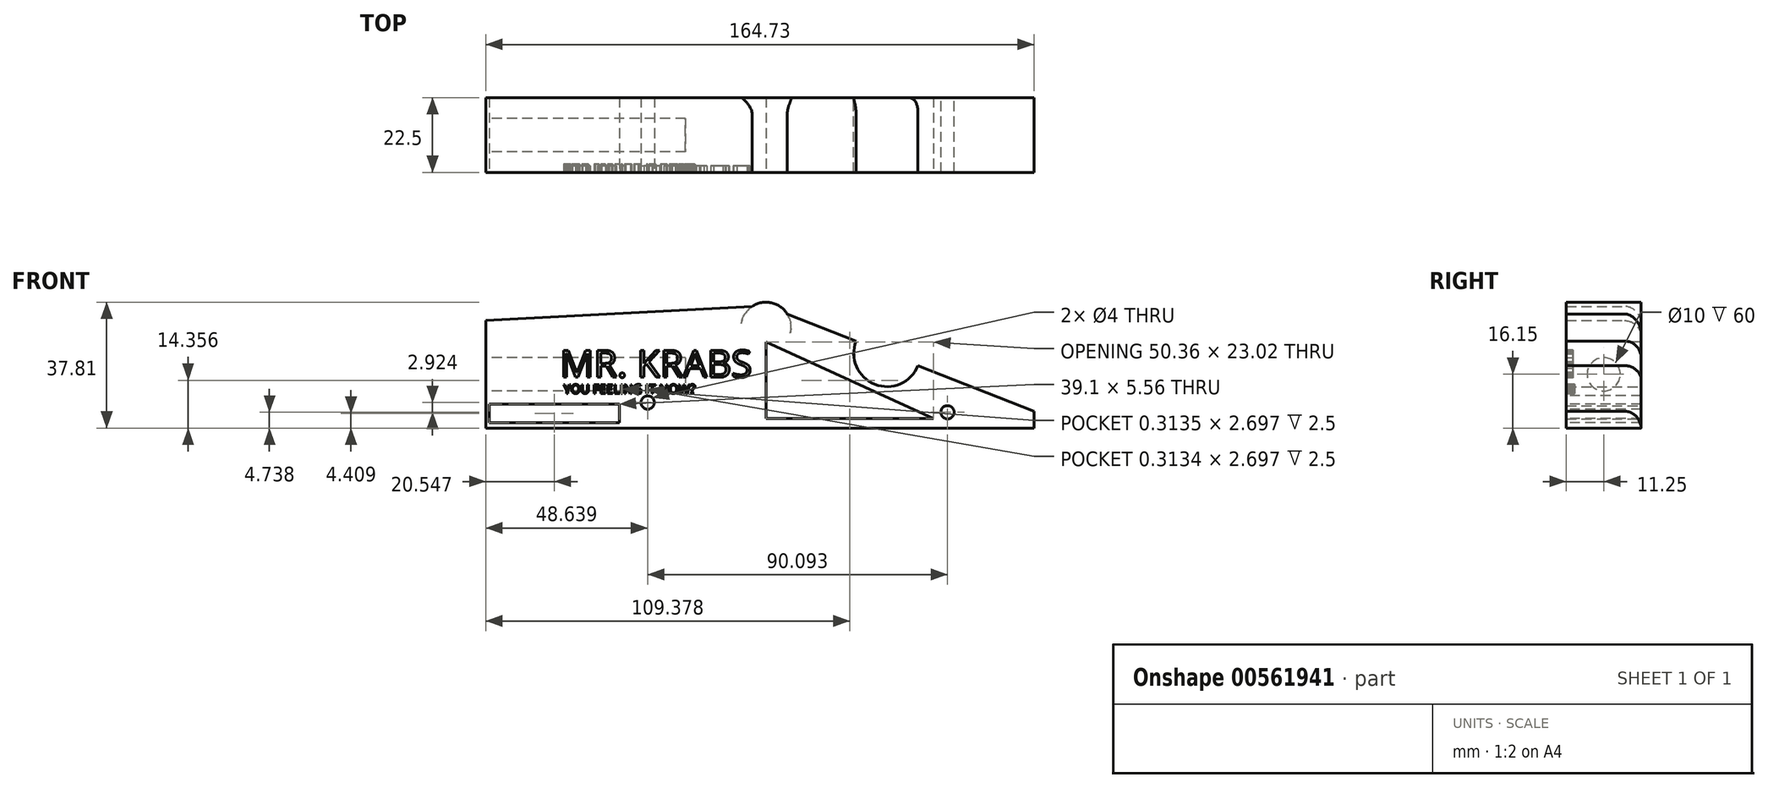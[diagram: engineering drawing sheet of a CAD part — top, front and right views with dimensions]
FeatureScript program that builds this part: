
annotation { "Feature Type Name" : "Feature", "Feature Type Description" : "" }
export const myFeature = defineFeature(function(context is Context, id is Id, definition is map)
    precondition{}
    {
        {
            var Q0;
            Q0=qCreatedBy(makeId("Front.planeOp"),FACE);
            var sketch = newSketch(context, id + "F0", { "sketchPlane" : qUnion([Q0])});
            skLineSegment(sketch, "E0.bottom", {"start": v(-84.2, -32.3) * mm, "end": v(215.8, -32.3) * mm});
            skLineSegment(sketch, "E0.top", {"start": v(-84.2, 37.7) * mm, "end": v(215.8, 37.7) * mm});
            skLineSegment(sketch, "E0.left", {"start": v(-84.2, -32.3) * mm, "end": v(-84.2, 37.7) * mm});
            skLineSegment(sketch, "E0.right", {"start": v(215.8, -32.3) * mm, "end": v(215.8, 37.7) * mm});
            skLineSegment(sketch, "E1", {"start": v(0, 4.48) * mm, "end": v(80.53, -27.27) * mm});
            skLineSegment(sketch, "E2", {"start": v(80.53, -27.27) * mm, "end": v(80.53, -32.3) * mm});
            skLineSegment(sketch, "E3", {"start": v(0, 4.48) * mm, "end": v(-84.2, 0) * mm});
            skPoint(sketch, "E3.endSnap0", {"position": v(-84.2, 2.7) * mm});
            skSolve(sketch);
        }
        {
            var Q0;
            Q0=makeQuery(id+"F0.imprint","IMPRINT",FACE,{"disambiguationData":[TD([[makeQuery(id+"F0.imprint","IMPRINT",EDGE,{"derivedFrom":sQuery(id+"F0.wireOp",EDGE,"E0.bottom")}),1.0]])]});
            extrude(context, id + "F1", {"entities" : qUnion([Q0]), "depth" : 40 * mm});
        }
        {
            var Q0;
            Q0=makeQuery(id+"F1.opExtrude","CAP_FACE",FACE,{"disambiguationData":[OSD([sQuery(id+"F0.wireOp",EDGE,"E0.bottom"),sQuery(id+"F0.wireOp",EDGE,"E0.top"),sQuery(id+"F0.wireOp",EDGE,"E0.left"),sQuery(id+"F0.wireOp",EDGE,"E0.right")])],"isStart":false});
            var sketch = newSketch(context, id + "F2", { "sketchPlane" : qUnion([Q0])});
            skCircle(sketch, "E4", {"center": v(-35.56, -24.64) * mm, "radius": 2 * mm});
            skCircle(sketch, "E5", {"center": v(174.33, -24.64) * mm, "radius": 2 * mm});
            skSolve(sketch);
        }
        {
            var Q0;
            Q0=makeQuery(id+"F2.imprint","IMPRINT",FACE,{"disambiguationData":[TD([[makeQuery(id+"F2.imprint","IMPRINT",EDGE,{"derivedFrom":sQuery(id+"F2.wireOp",EDGE,"E4")}),1.0]])]});
            var Q1;
            Q1=makeQuery(id+"F2.imprint","IMPRINT",FACE,{"disambiguationData":[TD([[makeQuery(id+"F2.imprint","IMPRINT",EDGE,{"derivedFrom":sQuery(id+"F2.wireOp",EDGE,"E5")}),1.0]])]});
            extrude(context, id + "F3", {"entities" : qUnion([Q0, Q1]), "operationType" : NewBodyOperationType.REMOVE, "endBound" : BoundingType.THROUGH_ALL, "oppositeDirection" : true, "depth" : 25 * mm});
        }
        {
            var Q0;
            Q0=makeQuery(id+"F2.imprint","IMPRINT",FACE,{"disambiguationData":[TD([[makeQuery(id+"F2.imprint","IMPRINT",EDGE,{"derivedFrom":sQuery(id+"F2.wireOp",EDGE,"E4")}),-1.0]])]});
            extrude(context, id + "F4", {"entities" : qUnion([Q0]), "operationType" : NewBodyOperationType.REMOVE, "oppositeDirection" : true, "depth" : 17.5 * mm, "offsetDistance" : 25 * mm});
        }
        {
            var Q0;
            Q0=makeQuery(id+"F1.opExtrude","SWEPT_FACE",FACE,{"disambiguationData":[OSD([sQuery(id+"F0.wireOp",EDGE,"E0.left")])]});
            var sketch = newSketch(context, id + "F5", { "sketchPlane" : qUnion([Q0])});
            skCircle(sketch, "E6", {"center": v(11.25, -16.15) * mm, "radius": 5 * mm});
            skPoint(sketch, "E6.centerSnap0", {"position": v(0, -16.15) * mm});
            skPoint(sketch, "E6.centerSnap1", {"position": v(11.25, -32.3) * mm});
            skSolve(sketch);
        }
        {
            var Q0;
            Q0=makeQuery(id+"F5.imprint","IMPRINT",FACE,{"disambiguationData":[TD([[makeQuery(id+"F5.imprint","IMPRINT",EDGE,{"derivedFrom":sQuery(id+"F5.wireOp",EDGE,"E6")}),1.0]])]});
            extrude(context, id + "F6", {"entities" : qUnion([Q0]), "operationType" : NewBodyOperationType.REMOVE, "oppositeDirection" : true, "depth" : 60 * mm, "offsetDistance" : 25 * mm});
        }
        {
            var Q0;
            Q0=makeQuery(id+"F1.opExtrude","CAP_FACE",FACE,{"disambiguationData":[OSD([sQuery(id+"F0.wireOp",EDGE,"E0.bottom"),sQuery(id+"F0.wireOp",EDGE,"E0.left"),sQuery(id+"F0.wireOp",EDGE,"E1"),sQuery(id+"F0.wireOp",EDGE,"E2"),sQuery(id+"F0.wireOp",EDGE,"E3")])],"isStart":true});
            var sketch = newSketch(context, id + "F7", { "sketchPlane" : qUnion([Q0])});
            skCircle(sketch, "E7", {"center": v(-36.37, -9.86) * mm, "radius": 10 * mm});
            skSolve(sketch);
        }
        {
            var Q0;
            {var subQ0=sQuery(id+"F7.wireOp",EDGE,"E7");var subQ1=makeQuery(id+"F1.opExtrude","CAP_EDGE",EDGE,{"disambiguationData":[OSD([sQuery(id+"F0.wireOp",EDGE,"E1")])],"isStart":true});var subQ2=makeQuery(id+"F7.imprint","INTERSECT",VERTEX,{"disambiguationData":[OD(0.0)],"derivedFrom":[subQ1,subQ0]});Q0=makeQuery(id+"F7.imprint","IMPRINT",FACE,{"disambiguationData":[TD([[makeQuery(id+"F7.imprint","IMPRINT",EDGE,{"disambiguationData":[TD([[subQ2,1.0]])],"derivedFrom":subQ0}),1.0]])]});}
            extrude(context, id + "F8", {"entities" : qUnion([Q0]), "operationType" : NewBodyOperationType.REMOVE, "endBound" : BoundingType.THROUGH_ALL, "oppositeDirection" : true, "depth" : 25 * mm, "offsetDistance" : 25 * mm});
        }
        {
            var Q0;
            Q0=makeQuery(id+"F1.opExtrude","CAP_FACE",FACE,{"disambiguationData":[OSD([sQuery(id+"F0.wireOp",EDGE,"E0.bottom"),sQuery(id+"F0.wireOp",EDGE,"E0.left"),sQuery(id+"F0.wireOp",EDGE,"E1"),sQuery(id+"F0.wireOp",EDGE,"E2"),sQuery(id+"F0.wireOp",EDGE,"E3")])],"isStart":true});
            var sketch = newSketch(context, id + "F9", { "sketchPlane" : qUnion([Q0])});
            skCircle(sketch, "E8", {"center": v(0, -1.99) * mm, "radius": 7.5 * mm});
            skSolve(sketch);
        }
        {
            var Q0;
            {var subQ0=sQuery(id+"F9.wireOp",EDGE,"E8");var subQ1=sQuery(id+"F0.wireOp",EDGE,"E3");var subQ2=makeQuery(id+"F1.opExtrude","CAP_EDGE",EDGE,{"disambiguationData":[OSD([subQ1])],"isStart":true});var subQ3=makeQuery(id+"F9.imprint","INTERSECT",VERTEX,{"derivedFrom":[subQ2,subQ0]});Q0=makeQuery(id+"F9.imprint","IMPRINT",FACE,{"disambiguationData":[TD([[makeQuery(id+"F9.imprint","IMPRINT",EDGE,{"disambiguationData":[TD([[subQ3,-1.0]])],"derivedFrom":subQ0}),1.0]])]});}
            extrude(context, id + "F10", {"entities" : qUnion([Q0]), "operationType" : NewBodyOperationType.ADD, "oppositeDirection" : true, "depth" : 22.5 * mm, "offsetDistance" : 25 * mm});
        }
        {
            var Q0;
            Q0=makeQuery(id+"F4.boolean.opBoolean","COPY",EDGE,{"derivedFrom":makeQuery(id+"F4.opExtrude","CAP_EDGE",EDGE,{"disambiguationData":[OSD([sQuery(id+"F0.wireOp",EDGE,"E3")])],"isStart":false})});
            var Q1;
            Q1=makeQuery(id+"F1.opExtrude","CAP_EDGE",EDGE,{"disambiguationData":[OSD([sQuery(id+"F0.wireOp",EDGE,"E3")])],"isStart":true});
            fillet(context, id + "F11", {"entities" : qUnion([Q0, Q1]), "radius" : 5 * mm, "tangentPropagation" : true, "allowEdgeOverflow" : false});
        }
        {
            var Q0;
            {var subQ0=sQuery(id+"F0.wireOp",EDGE,"E1");var subQ1=sQuery(id+"F0.wireOp",EDGE,"E2");Q0=makeQuery(id+"F8.boolean.opBoolean","SPLIT",EDGE,{"disambiguationData":[TD([makeQuery(id+"F1.opExtrude","SWEPT_FACE",FACE,{"disambiguationData":[OSD([subQ1])]})])],"derivedFrom":makeQuery(id+"F4.boolean.opBoolean","COPY",EDGE,{"derivedFrom":makeQuery(id+"F4.opExtrude","CAP_EDGE",EDGE,{"disambiguationData":[OSD([subQ0])],"isStart":false})})});}
            var Q1;
            {var subQ0=sQuery(id+"F0.wireOp",EDGE,"E2");var subQ1=sQuery(id+"F0.wireOp",EDGE,"E1");Q1=makeQuery(id+"F8.boolean.opBoolean","SPLIT",EDGE,{"disambiguationData":[TD([makeQuery(id+"F1.opExtrude","SWEPT_FACE",FACE,{"disambiguationData":[OSD([subQ0])]})])],"derivedFrom":makeQuery(id+"F1.opExtrude","CAP_EDGE",EDGE,{"disambiguationData":[OSD([subQ1])],"isStart":true})});}
            var Q2;
            {var subQ0=sQuery(id+"F0.wireOp",EDGE,"E3");var subQ1=sQuery(id+"F0.wireOp",EDGE,"E1");Q2=makeQuery(id+"F8.boolean.opBoolean","SPLIT",EDGE,{"disambiguationData":[TD([makeQuery(id+"F1.opExtrude","SWEPT_FACE",FACE,{"disambiguationData":[OSD([subQ0])]})])],"derivedFrom":makeQuery(id+"F1.opExtrude","CAP_EDGE",EDGE,{"disambiguationData":[OSD([subQ1])],"isStart":true})});}
            var Q3;
            {var subQ0=sQuery(id+"F0.wireOp",EDGE,"E1");var subQ1=sQuery(id+"F0.wireOp",EDGE,"E3");Q3=makeQuery(id+"F8.boolean.opBoolean","SPLIT",EDGE,{"disambiguationData":[TD([makeQuery(id+"F1.opExtrude","SWEPT_FACE",FACE,{"disambiguationData":[OSD([subQ1])]})])],"derivedFrom":makeQuery(id+"F4.boolean.opBoolean","COPY",EDGE,{"derivedFrom":makeQuery(id+"F4.opExtrude","CAP_EDGE",EDGE,{"disambiguationData":[OSD([subQ0])],"isStart":false})})});}
            fillet(context, id + "F12", {"entities" : qUnion([Q0, Q1, Q2, Q3]), "radius" : 5 * mm, "tangentPropagation" : true, "allowEdgeOverflow" : false});
        }
        {
            var Q0;
            {var subQ0=sQuery(id+"F0.wireOp",EDGE,"E3");var subQ1=sQuery(id+"F0.wireOp",EDGE,"E1");Q0=makeQuery(id+"F10.boolean.opBoolean","MERGE",FACE,{"derivedFrom":[makeQuery(id+"F4.boolean.opBoolean","COPY",FACE,{"derivedFrom":makeQuery(id+"F4.opExtrude","CAP_FACE",FACE,{"disambiguationData":[OSD([sQuery(id+"F0.wireOp",EDGE,"E0.bottom"),sQuery(id+"F0.wireOp",EDGE,"E0.left"),subQ1,sQuery(id+"F0.wireOp",EDGE,"E2"),subQ0,sQuery(id+"F2.wireOp",EDGE,"E4")])],"isStart":false})}),makeQuery(id+"F10.opExtrude","CAP_FACE",FACE,{"disambiguationData":[OSD([subQ1,subQ0,sQuery(id+"F9.wireOp",EDGE,"E8")])],"isStart":false})]});}
            var sketch = newSketch(context, id + "F13", { "sketchPlane" : qUnion([Q0])});
            skText(sketch, "E9", { "text": "MR. KRABS", "fontName": "OpenSans-Regular.ttf"});
            const initialGuessF13  = {"E9": [-0.0619, -0.01702, 1, 0, 0.00813]};
            skSetInitialGuess(sketch, initialGuessF13);
            skSolve(sketch);
        }
        {
            var Q0;
            Q0=qSketchRegion(id+"F13",true);
            extrude(context, id + "F14", {"entities" : qUnion([Q0]), "operationType" : NewBodyOperationType.REMOVE, "oppositeDirection" : true, "depth" : 2 * mm, "offsetDistance" : 25 * mm});
        }
        {
            var Q0;
            {var subQ0=sQuery(id+"F0.wireOp",EDGE,"E3");var subQ1=sQuery(id+"F0.wireOp",EDGE,"E1");Q0=makeQuery(id+"F10.boolean.opBoolean","MERGE",FACE,{"derivedFrom":[makeQuery(id+"F1.opExtrude","CAP_FACE",FACE,{"disambiguationData":[OSD([sQuery(id+"F0.wireOp",EDGE,"E0.bottom"),sQuery(id+"F0.wireOp",EDGE,"E0.left"),subQ1,sQuery(id+"F0.wireOp",EDGE,"E2"),subQ0])],"isStart":true}),makeQuery(id+"F10.opExtrude","CAP_FACE",FACE,{"disambiguationData":[OSD([subQ1,subQ0,sQuery(id+"F9.wireOp",EDGE,"E8")])],"isStart":true})]});}
            var sketch = newSketch(context, id + "F15", { "sketchPlane" : qUnion([Q0])});
            skSolve(sketch);
        }
        {
            var Q0;
            {var subQ1=sQuery(id+"F0.wireOp",EDGE,"E0.left");Q0=makeQuery(id+"F15.imprint","IMPRINT",FACE,{"disambiguationData":[TD([[makeQuery(id+"F15.imprint","IMPRINT",EDGE,{"derivedFrom":makeQuery(id+"F1.opExtrude","CAP_EDGE",EDGE,{"disambiguationData":[OSD([subQ1])],"isStart":true})}),1.0]])]});}
            var sketch = newSketch(context, id + "F16", { "sketchPlane" : qUnion([Q0])});
            skCircle(sketch, "E10", {"center": v(-54.53, -27.56) * mm, "radius": 2 * mm});
            skSolve(sketch);
        }
        {
            var Q0;
            Q0=makeQuery(id+"F16.imprint","IMPRINT",FACE,{"disambiguationData":[TD([[makeQuery(id+"F16.imprint","IMPRINT",EDGE,{"derivedFrom":sQuery(id+"F16.wireOp",EDGE,"E10")}),1.0]])]});
            extrude(context, id + "F17", {"entities" : qUnion([Q0]), "operationType" : NewBodyOperationType.REMOVE, "endBound" : BoundingType.THROUGH_ALL, "oppositeDirection" : true, "depth" : 25 * mm, "offsetDistance" : 25 * mm});
        }
        {
            var Q0;
            {var subQ0=sQuery(id+"F0.wireOp",EDGE,"E3");var subQ1=sQuery(id+"F9.wireOp",EDGE,"E8");var subQ2=sQuery(id+"F2.wireOp",EDGE,"E4");var subQ3=sQuery(id+"F0.wireOp",EDGE,"E1");var subQ5=sQuery(id+"F0.wireOp",EDGE,"E2");var subQ6=sQuery(id+"F0.wireOp",EDGE,"E0.left");var subQ7=sQuery(id+"F0.wireOp",EDGE,"E0.bottom");var subQ8=makeQuery(id+"F4.boolean.opBoolean","COPY",FACE,{"derivedFrom":makeQuery(id+"F4.opExtrude","CAP_FACE",FACE,{"disambiguationData":[OSD([subQ7,subQ6,subQ3,subQ5,subQ0,subQ2])],"isStart":false})});Q0=makeQuery(id+"F14.boolean.opBoolean","SPLIT",FACE,{"disambiguationData":[TD([makeQuery(id+"F1.opExtrude","SWEPT_FACE",FACE,{"disambiguationData":[OSD([subQ7])]})])],"derivedFrom":makeQuery(id+"F10.boolean.opBoolean","MERGE",FACE,{"derivedFrom":[subQ8,makeQuery(id+"F10.opExtrude","CAP_FACE",FACE,{"disambiguationData":[OSD([subQ3,subQ0,subQ1])],"isStart":false})]})});}
            var sketch = newSketch(context, id + "F18", { "sketchPlane" : qUnion([Q0])});
            skLineSegment(sketch, "E11", {"start": v(0, -6.43) * mm, "end": v(0, -29.46) * mm});
            skLineSegment(sketch, "E12", {"start": v(0, -29.46) * mm, "end": v(50.36, -29.46) * mm});
            skLineSegment(sketch, "E13", {"start": v(50.36, -29.46) * mm, "end": v(0, -6.43) * mm});
            skSolve(sketch);
        }
        {
            var Q0;
            Q0=makeQuery(id+"F18.imprint","IMPRINT",FACE,{"disambiguationData":[TD([[makeQuery(id+"F18.imprint","IMPRINT",EDGE,{"derivedFrom":sQuery(id+"F18.wireOp",EDGE,"E11")}),1.0]])]});
            extrude(context, id + "F19", {"entities" : qUnion([Q0]), "operationType" : NewBodyOperationType.REMOVE, "endBound" : BoundingType.THROUGH_ALL, "oppositeDirection" : true, "depth" : 25 * mm, "offsetDistance" : 25 * mm});
        }
        {
            var Q0;
            {var subQ0=sQuery(id+"F0.wireOp",EDGE,"E3");var subQ1=sQuery(id+"F9.wireOp",EDGE,"E8");var subQ2=sQuery(id+"F2.wireOp",EDGE,"E4");var subQ3=sQuery(id+"F0.wireOp",EDGE,"E1");var subQ5=sQuery(id+"F0.wireOp",EDGE,"E2");var subQ6=sQuery(id+"F0.wireOp",EDGE,"E0.left");var subQ7=sQuery(id+"F0.wireOp",EDGE,"E0.bottom");var subQ8=makeQuery(id+"F4.boolean.opBoolean","COPY",FACE,{"derivedFrom":makeQuery(id+"F4.opExtrude","CAP_FACE",FACE,{"disambiguationData":[OSD([subQ7,subQ6,subQ3,subQ5,subQ0,subQ2])],"isStart":false})});Q0=makeQuery(id+"F14.boolean.opBoolean","SPLIT",FACE,{"disambiguationData":[TD([makeQuery(id+"F1.opExtrude","SWEPT_FACE",FACE,{"disambiguationData":[OSD([subQ7])]})])],"derivedFrom":makeQuery(id+"F10.boolean.opBoolean","MERGE",FACE,{"derivedFrom":[subQ8,makeQuery(id+"F10.opExtrude","CAP_FACE",FACE,{"disambiguationData":[OSD([subQ3,subQ0,subQ1])],"isStart":false})]})});}
            var sketch = newSketch(context, id + "F20", { "sketchPlane" : qUnion([Q0])});
            skText(sketch, "E14", { "text": "YOU FEELING IT NOW?\n", "fontName": "OpenSans-Regular.ttf"});
            const initialGuessF20  = {"E14": [-0.0608, -0.02191, 1, 0, 0.00272]};
            skSetInitialGuess(sketch, initialGuessF20);
            skSolve(sketch);
        }
        {
            var Q0;
            Q0=qSketchRegion(id+"F20",true);
            extrude(context, id + "F21", {"entities" : qUnion([Q0]), "operationType" : NewBodyOperationType.REMOVE, "oppositeDirection" : true, "depth" : 2.5 * mm, "offsetDistance" : 25 * mm});
        }
        {
            var Q0;
            {var subQ49=sQuery(id+"F9.wireOp",EDGE,"E8");var subQ63=sQuery(id+"F0.wireOp",EDGE,"E1");var subQ65=sQuery(id+"F0.wireOp",EDGE,"E3");var subQ66=sQuery(id+"F2.wireOp",EDGE,"E4");var subQ67=sQuery(id+"F0.wireOp",EDGE,"E2");var subQ68=sQuery(id+"F0.wireOp",EDGE,"E0.left");var subQ69=sQuery(id+"F0.wireOp",EDGE,"E0.bottom");var subQ70=makeQuery(id+"F4.boolean.opBoolean","COPY",FACE,{"derivedFrom":makeQuery(id+"F4.opExtrude","CAP_FACE",FACE,{"disambiguationData":[OSD([subQ69,subQ68,subQ63,subQ67,subQ65,subQ66])],"isStart":false})});var subQ83=makeQuery(id+"F1.opExtrude","SWEPT_FACE",FACE,{"disambiguationData":[OSD([subQ69])]});Q0=makeQuery(id+"F21.boolean.opBoolean","SPLIT",FACE,{"disambiguationData":[TD([subQ83])],"derivedFrom":makeQuery(id+"F14.boolean.opBoolean","SPLIT",FACE,{"disambiguationData":[TD([subQ83])],"derivedFrom":makeQuery(id+"F10.boolean.opBoolean","MERGE",FACE,{"derivedFrom":[subQ70,makeQuery(id+"F10.opExtrude","CAP_FACE",FACE,{"disambiguationData":[OSD([subQ63,subQ65,subQ49])],"isStart":false})]})})});}
            var sketch = newSketch(context, id + "F22", { "sketchPlane" : qUnion([Q0])});
            skLineSegment(sketch, "E15.bottom", {"start": v(-83.2, -25.11) * mm, "end": v(-44.1, -25.11) * mm});
            skLineSegment(sketch, "E15.top", {"start": v(-83.2, -30.67) * mm, "end": v(-44.1, -30.67) * mm});
            skLineSegment(sketch, "E15.left", {"start": v(-83.2, -25.11) * mm, "end": v(-83.2, -30.67) * mm});
            skLineSegment(sketch, "E15.right", {"start": v(-44.1, -25.11) * mm, "end": v(-44.1, -30.67) * mm});
            skSolve(sketch);
        }
        {
            var Q0;
            Q0=makeQuery(id+"F22.imprint","IMPRINT",FACE,{"disambiguationData":[TD([[makeQuery(id+"F22.imprint","IMPRINT",EDGE,{"derivedFrom":sQuery(id+"F22.wireOp",EDGE,"E15.bottom")}),-1.0]])]});
            extrude(context, id + "F23", {"entities" : qUnion([Q0]), "operationType" : NewBodyOperationType.REMOVE, "endBound" : BoundingType.THROUGH_ALL, "oppositeDirection" : true, "depth" : 25 * mm, "offsetDistance" : 25 * mm});
        }
    });
